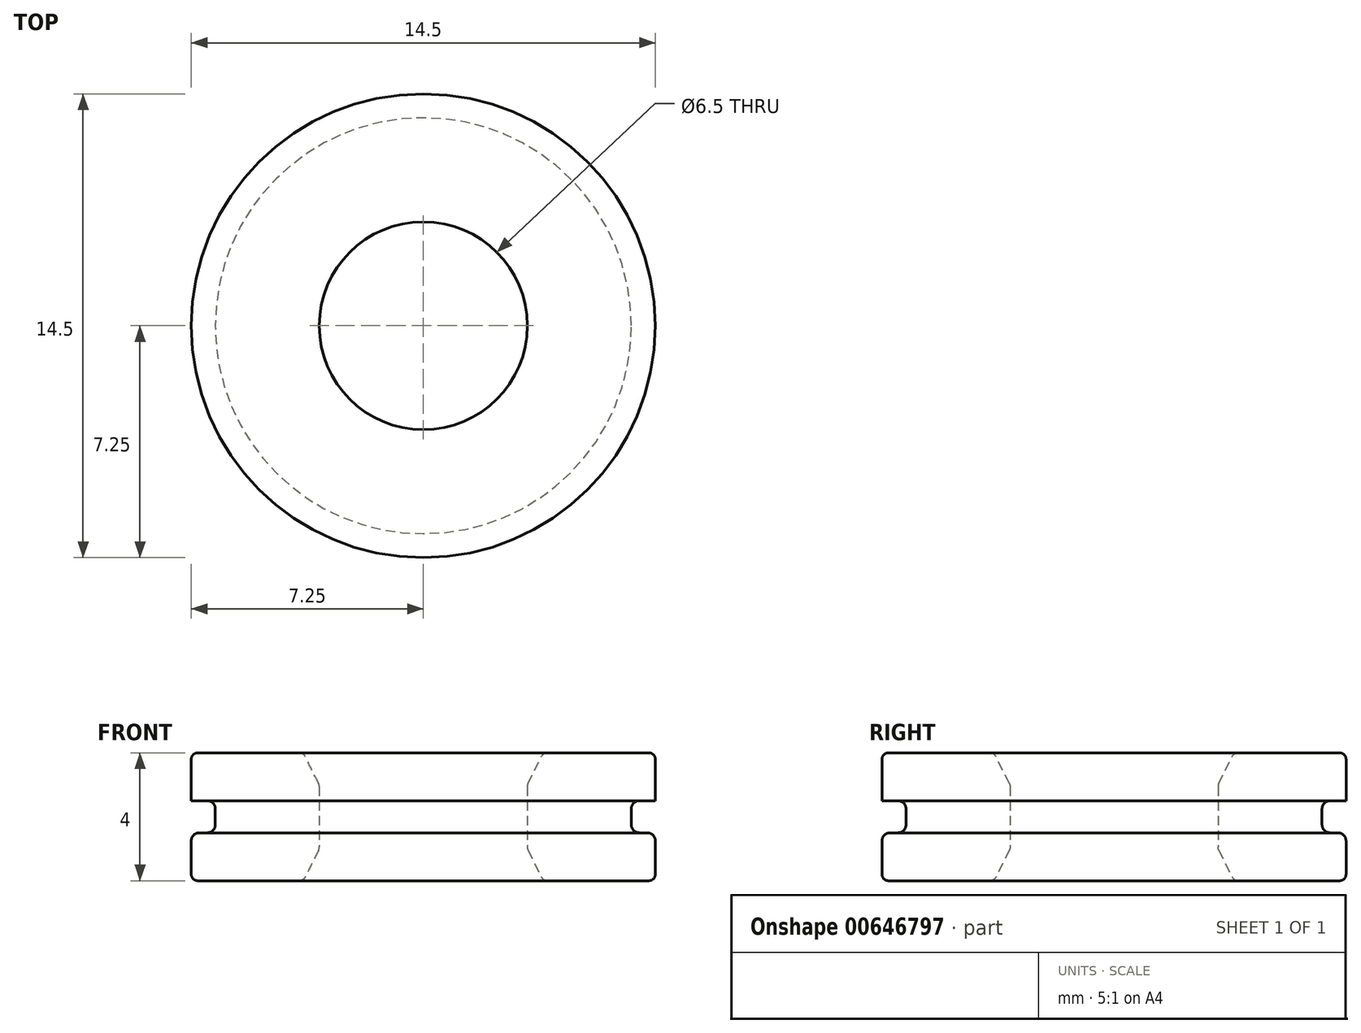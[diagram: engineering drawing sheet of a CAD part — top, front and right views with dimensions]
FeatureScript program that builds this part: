
annotation { "Feature Type Name" : "Feature", "Feature Type Description" : "" }
export const myFeature = defineFeature(function(context is Context, id is Id, definition is map)
    precondition{}
    {
        {
            var Q0;
            Q0=qCreatedBy(makeId("Top.planeOp"),FACE);
            var sketch = newSketch(context, id + "F0", { "sketchPlane" : qUnion([Q0])});
            skCircle(sketch, "E0", {"center": v(0, 0) * mm, "radius": 7.25 * mm});
            skCircle(sketch, "E1", {"center": v(0, 0) * mm, "radius": 3.25 * mm});
            skCircle(sketch, "E2", {"center": v(0, 0) * mm, "radius": 6.5 * mm});
            skSolve(sketch);
        }
        {
            var Q0;
            Q0=makeQuery(id+"F0.imprint","IMPRINT",FACE,{"disambiguationData":[TD([[makeQuery(id+"F0.imprint","IMPRINT",EDGE,{"derivedFrom":sQuery(id+"F0.wireOp",EDGE,"E0")}),1.0]])]});
            var Q1;
            Q1=makeQuery(id+"F0.imprint","IMPRINT",FACE,{"disambiguationData":[TD([[makeQuery(id+"F0.imprint","IMPRINT",EDGE,{"derivedFrom":sQuery(id+"F0.wireOp",EDGE,"E1")}),-1.0]])]});
            extrude(context, id + "F1", {"entities" : qUnion([Q0, Q1]), "depth" : 4 * mm, "offsetDistance" : 25 * mm});
        }
        {
            var Q0;
            Q0=makeQuery(id+"F1.opExtrude","CAP_EDGE",EDGE,{"disambiguationData":[OSD([sQuery(id+"F0.wireOp",EDGE,"E0")])],"isStart":false});
            var Q1;
            Q1=makeQuery(id+"F1.opExtrude","CAP_EDGE",EDGE,{"disambiguationData":[OSD([sQuery(id+"F0.wireOp",EDGE,"E0")])],"isStart":true});
            fillet(context, id + "F2", {"entities" : qUnion([Q0, Q1]), "radius" : .2 * mm, "tangentPropagation" : true, "allowEdgeOverflow" : false});
        }
        {
            var Q0;
            Q0=makeQuery(id+"F1.opExtrude","CAP_EDGE",EDGE,{"disambiguationData":[OSD([sQuery(id+"F0.wireOp",EDGE,"E1")])],"isStart":false});
            var Q1;
            Q1=makeQuery(id+"F1.opExtrude","CAP_EDGE",EDGE,{"disambiguationData":[OSD([sQuery(id+"F0.wireOp",EDGE,"E1")])],"isStart":true});
            chamfer(context, id + "F3", {"entities" : qUnion([Q0, Q1]), "chamferType" : ChamferType.TWO_OFFSETS, "width1" : 0.5 * mm, "oppositeDirection" : true, "width2" : 1 * mm, "tangentPropagation" : true});
        }
        {
            var Q0;
            {var subQ0=sQuery(id+"F0.wireOp",EDGE,"E1");Q0=makeQuery(id+"F3.opChamfer","BLEND_EDGE",EDGE,{"blendedFrom":[makeQuery(id+"F1.opExtrude","CAP_EDGE",EDGE,{"disambiguationData":[OSD([subQ0])],"isStart":false}),makeQuery(id+"F1.opExtrude","CAP_FACE",FACE,{"disambiguationData":[OSD([sQuery(id+"F0.wireOp",EDGE,"E0"),subQ0])],"isStart":false})],"blendedInto":[makeQuery(id+"F1.opExtrude","CAP_FACE",FACE,{"disambiguationData":[OSD([sQuery(id+"F0.wireOp",EDGE,"E0"),subQ0])],"isStart":false})]});}
            var Q1;
            {var subQ0=sQuery(id+"F0.wireOp",EDGE,"E1");Q1=makeQuery(id+"F3.opChamfer","BLEND_EDGE",EDGE,{"blendedFrom":[makeQuery(id+"F1.opExtrude","CAP_EDGE",EDGE,{"disambiguationData":[OSD([subQ0])],"isStart":false}),makeQuery(id+"F1.opExtrude","SWEPT_FACE",FACE,{"disambiguationData":[OSD([subQ0])]})],"blendedInto":[makeQuery(id+"F1.opExtrude","SWEPT_FACE",FACE,{"disambiguationData":[OSD([subQ0])]})]});}
            var Q2;
            {var subQ0=sQuery(id+"F0.wireOp",EDGE,"E1");Q2=makeQuery(id+"F3.opChamfer","BLEND_EDGE",EDGE,{"blendedFrom":[makeQuery(id+"F1.opExtrude","CAP_EDGE",EDGE,{"disambiguationData":[OSD([subQ0])],"isStart":true}),makeQuery(id+"F1.opExtrude","SWEPT_FACE",FACE,{"disambiguationData":[OSD([subQ0])]})],"blendedInto":[makeQuery(id+"F1.opExtrude","SWEPT_FACE",FACE,{"disambiguationData":[OSD([subQ0])]})]});}
            var Q3;
            {var subQ0=sQuery(id+"F0.wireOp",EDGE,"E1");Q3=makeQuery(id+"F3.opChamfer","BLEND_FACE",FACE,{"disambiguationData":[OSD([subQ0]),TDD([makeQuery(id+"F1.opExtrude","CAP_EDGE",EDGE,{"disambiguationData":[OSD([subQ0])],"isStart":true})])]});}
            fillet(context, id + "F4", {"entities" : qUnion([Q0, Q1, Q2, Q3]), "radius" : .2 * mm, "tangentPropagation" : true, "allowEdgeOverflow" : false});
        }
        {
            var Q0;
            Q0=makeQuery(id+"F0.imprint","IMPRINT",FACE,{"disambiguationData":[TD([[makeQuery(id+"F0.imprint","IMPRINT",EDGE,{"derivedFrom":sQuery(id+"F0.wireOp",EDGE,"E0")}),1.0]])]});
            extrude(context, id + "F5", {"entities" : qUnion([Q0]), "operationType" : NewBodyOperationType.REMOVE, "depth" : 2.5 * mm, "offsetDistance" : 25 * mm, "hasSecondDirection" : true, "secondDirectionOppositeDirection" : false, "secondDirectionDepth" : 1.5 * mm});
        }
        {
            var Q0;
            Q0=makeQuery(id+"F5.boolean.opBoolean","COPY",EDGE,{"derivedFrom":makeQuery(id+"F5.opExtrude","CAP_EDGE",EDGE,{"disambiguationData":[OSD([sQuery(id+"F0.wireOp",EDGE,"E0")])],"isStart":false})});
            var Q1;
            Q1=makeQuery(id+"F5.boolean.opBoolean","COPY",EDGE,{"derivedFrom":makeQuery(id+"F5.opExtrude","CAP_EDGE",EDGE,{"disambiguationData":[OSD([sQuery(id+"F0.wireOp",EDGE,"E0")])],"isStart":true})});
            var Q2;
            Q2=makeQuery(id+"F5.boolean.opBoolean","COPY",EDGE,{"derivedFrom":makeQuery(id+"F5.opExtrude","CAP_EDGE",EDGE,{"disambiguationData":[OSD([sQuery(id+"F0.wireOp",EDGE,"E2")])],"isStart":true})});
            var Q3;
            Q3=makeQuery(id+"F5.boolean.opBoolean","COPY",EDGE,{"derivedFrom":makeQuery(id+"F5.opExtrude","CAP_EDGE",EDGE,{"disambiguationData":[OSD([sQuery(id+"F0.wireOp",EDGE,"E2")])],"isStart":false})});
            fillet(context, id + "F6", {"entities" : qUnion([Q0, Q1, Q2, Q3]), "radius" : .25 * mm, "tangentPropagation" : true, "allowEdgeOverflow" : false});
        }
    });
